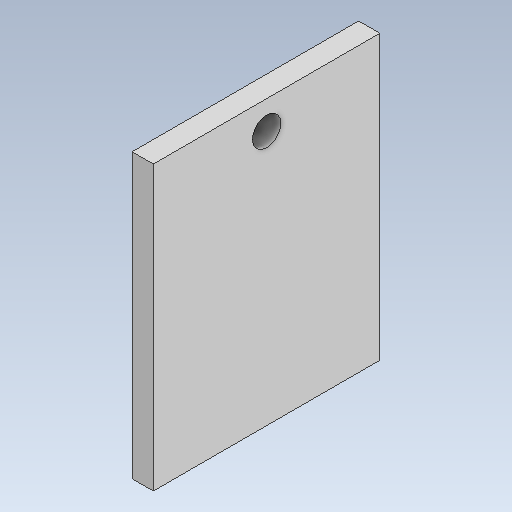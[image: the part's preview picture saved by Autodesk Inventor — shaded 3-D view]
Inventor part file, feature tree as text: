
AUTODESK INVENTOR PART (.ipt)
format: ipt  version: 2021 (Build 250183000, 183)  size: 100,352 bytes
history: native  units: in
note: dims shown in document units (in); Inventor stores cm internally (conversion verified against a paired STEP export)
features: other x3, sketch x2, plane x1
ambient origin geometry x8: Origin, YZ Plane, XZ Plane, XY Plane, X Axis, Y Axis, Z Axis, Center Point
bodies: Solid1 (feature_tree)
feature tree (6):
  other  "woodForAssemblyLeftSide.ipt"
  other  "Solid1::woodForAssemblyLeftSide.ipt"
  other  "TaggingFeature1"
  sketch  "Sketch1"  dims[d0=0.3937in]
  sketch  "Sketch2"
  plane  "Work Plane1"
